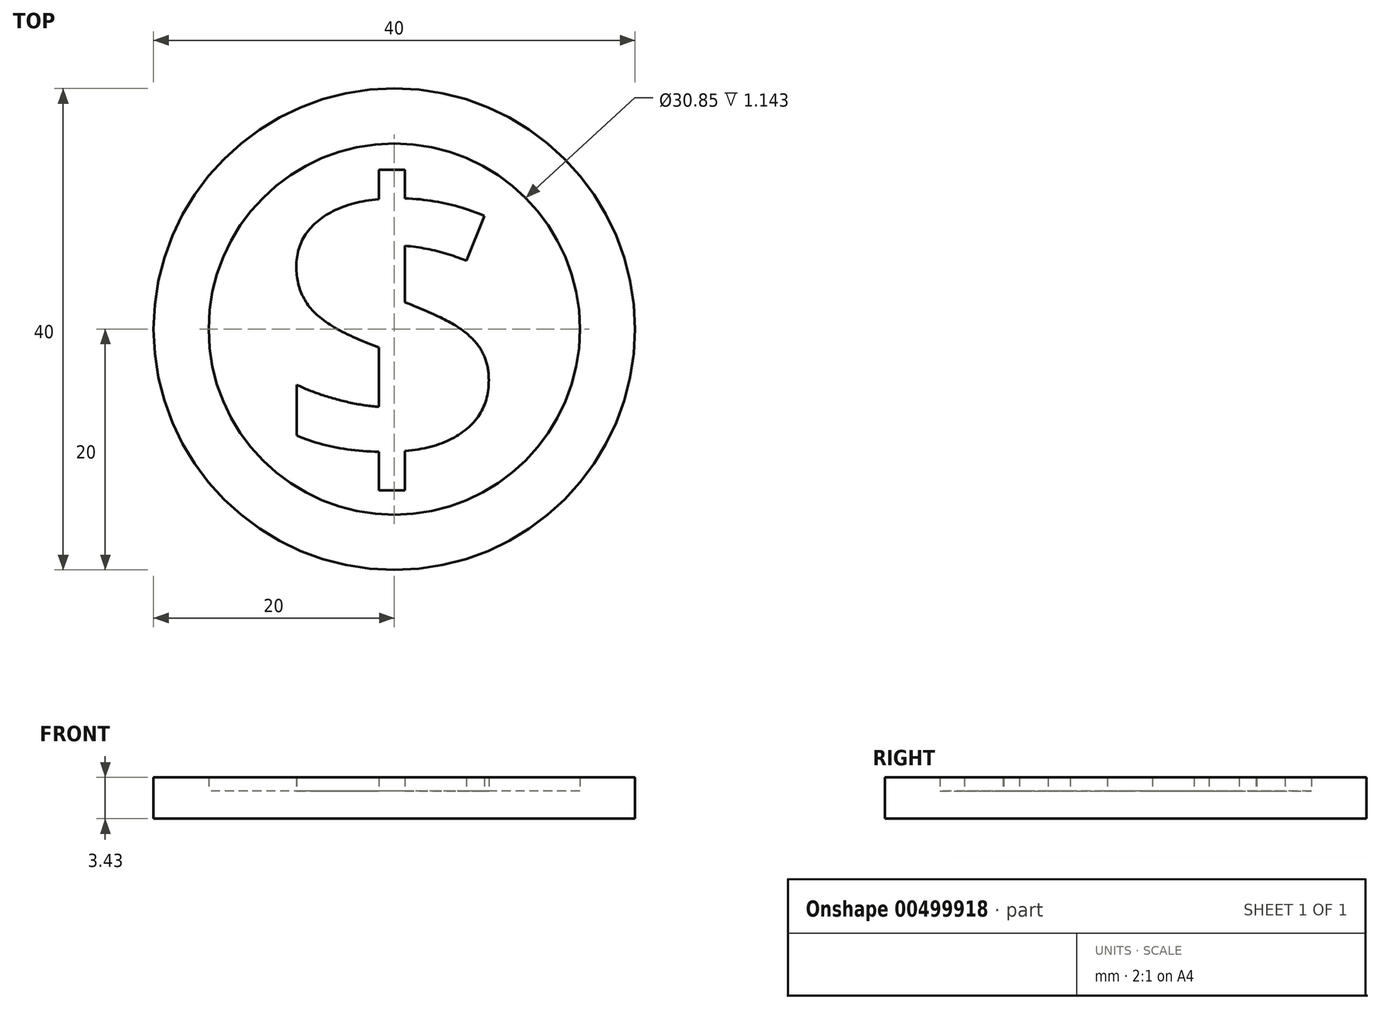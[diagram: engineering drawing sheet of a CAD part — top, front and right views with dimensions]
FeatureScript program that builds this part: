
annotation { "Feature Type Name" : "Feature", "Feature Type Description" : "" }
export const myFeature = defineFeature(function(context is Context, id is Id, definition is map)
    precondition{}
    {
        {
            var Q0;
            Q0=qCreatedBy(makeId("Top.planeOp"),FACE);
            var sketch = newSketch(context, id + "F0", { "sketchPlane" : qUnion([Q0])});
            skCircle(sketch, "E0", {"center": v(0, 0) * mm, "radius": 20 * mm});
            skSolve(sketch);
        }
        {
            var Q0;
            Q0 = qSketchRegion(id + "F0", true);
            extrude(context, id + "F1", {"entities" : qUnion([Q0]), "depth" : 2.3 * mm});
        }
        {
            var Q0;
            Q0=makeQuery(id+"F1.opExtrude","CAP_FACE",FACE,{"disambiguationData":[OSD([sQuery(id+"F0.wireOp",EDGE,"E0")])],"isStart":false});
            var sketch = newSketch(context, id + "F2", { "sketchPlane" : qUnion([Q0])});
            skText(sketch, "E1", { "text": "$", "fontName": "OpenSans-Bold.ttf"});
            const initialGuessF2  = {"E1": [-0.00954, -0.0115, 1, 0, 0.02348]};
            skSetInitialGuess(sketch, initialGuessF2);
            skSolve(sketch);
        }
        {
            var Q0;
            Q0 = qSketchRegion(id + "F2", true);
            extrude(context, id + "F3", {"entities" : qUnion([Q0]), "operationType" : NewBodyOperationType.ADD, "depth" : 1.14 * mm});
        }
        {
            var Q0;
            {var subQ0=sQuery(id+"F0.wireOp",EDGE,"E0");Q0=makeQuery(id+"F3.boolean.opBoolean","SPLIT",FACE,{"disambiguationData":[TD([makeQuery(id+"F1.opExtrude","SWEPT_FACE",FACE,{"disambiguationData":[OSD([subQ0])]})])],"derivedFrom":makeQuery(id+"F1.opExtrude","CAP_FACE",FACE,{"disambiguationData":[OSD([subQ0])],"isStart":false})});}
            var sketch = newSketch(context, id + "F4", { "sketchPlane" : qUnion([Q0])});
            skCircle(sketch, "E2.0", {"center": v(0, 0) * mm, "radius": 20 * mm});
            skCircle(sketch, "E3", {"center": v(0, 0) * mm, "radius": 15.42 * mm});
            skSolve(sketch);
        }
        {
            var Q0;
            Q0 = qSketchRegion(id + "F4", true);
            var Q1;
            Q1=makeQuery(id+"F3.opExtrude","CAP_FACE",FACE,{"disambiguationData":[OSD([sQuery(id+"F2.wireOp",EDGE,"E1.sketch_text.stroke-0"),sQuery(id+"F2.wireOp",EDGE,"E1.sketch_text.stroke-1"),sQuery(id+"F2.wireOp",EDGE,"E1.sketch_text.stroke-2"),sQuery(id+"F2.wireOp",EDGE,"E1.sketch_text.stroke-3"),sQuery(id+"F2.wireOp",EDGE,"E1.sketch_text.stroke-4"),sQuery(id+"F2.wireOp",EDGE,"E1.sketch_text.stroke-5"),sQuery(id+"F2.wireOp",EDGE,"E1.sketch_text.stroke-6"),sQuery(id+"F2.wireOp",EDGE,"E1.sketch_text.stroke-7"),sQuery(id+"F2.wireOp",EDGE,"E1.sketch_text.stroke-8"),sQuery(id+"F2.wireOp",EDGE,"E1.sketch_text.stroke-9"),sQuery(id+"F2.wireOp",EDGE,"E1.sketch_text.stroke-10"),sQuery(id+"F2.wireOp",EDGE,"E1.sketch_text.stroke-11"),sQuery(id+"F2.wireOp",EDGE,"E1.sketch_text.stroke-12"),sQuery(id+"F2.wireOp",EDGE,"E1.sketch_text.stroke-13"),sQuery(id+"F2.wireOp",EDGE,"E1.sketch_text.stroke-14"),sQuery(id+"F2.wireOp",EDGE,"E1.sketch_text.stroke-15"),sQuery(id+"F2.wireOp",EDGE,"E1.sketch_text.stroke-16"),sQuery(id+"F2.wireOp",EDGE,"E1.sketch_text.stroke-17"),sQuery(id+"F2.wireOp",EDGE,"E1.sketch_text.stroke-18"),sQuery(id+"F2.wireOp",EDGE,"E1.sketch_text.stroke-19"),sQuery(id+"F2.wireOp",EDGE,"E1.sketch_text.stroke-20"),sQuery(id+"F2.wireOp",EDGE,"E1.sketch_text.stroke-21"),sQuery(id+"F2.wireOp",EDGE,"E1.sketch_text.stroke-22"),sQuery(id+"F2.wireOp",EDGE,"E1.sketch_text.stroke-23"),sQuery(id+"F2.wireOp",EDGE,"E1.sketch_text.stroke-24"),sQuery(id+"F2.wireOp",EDGE,"E1.sketch_text.stroke-25"),sQuery(id+"F2.wireOp",EDGE,"E1.sketch_text.stroke-26"),sQuery(id+"F2.wireOp",EDGE,"E1.sketch_text.stroke-27"),sQuery(id+"F2.wireOp",EDGE,"E1.sketch_text.stroke-28"),sQuery(id+"F2.wireOp",EDGE,"E1.sketch_text.stroke-29"),sQuery(id+"F2.wireOp",EDGE,"E1.sketch_text.stroke-30"),sQuery(id+"F2.wireOp",EDGE,"E1.sketch_text.stroke-31"),sQuery(id+"F2.wireOp",EDGE,"E1.sketch_text.stroke-32")])],"isStart":false});
            extrude(context, id + "F5", {"entities" : qUnion([Q0]), "operationType" : NewBodyOperationType.ADD, "endBound" : BoundingType.UP_TO_SURFACE, "endBoundEntityFace" : qUnion([Q1]), "depth" : 3.17 * mm});
        }
        {
            var Q0;
            Q0=makeQuery(id+"F3.boolean.opBoolean","SPLIT",FACE,{"disambiguationData":[TD([makeQuery(id+"F3.opExtrude","SWEPT_FACE",FACE,{"disambiguationData":[OSD([sQuery(id+"F2.wireOp",EDGE,"E1.sketch_text.stroke-29")])]})])],"derivedFrom":makeQuery(id+"F1.opExtrude","CAP_FACE",FACE,{"disambiguationData":[OSD([sQuery(id+"F0.wireOp",EDGE,"E0")])],"isStart":false})});
            var Q1;
            Q1=makeQuery(id+"F3.boolean.opBoolean","SPLIT",FACE,{"disambiguationData":[TD([makeQuery(id+"F3.opExtrude","SWEPT_FACE",FACE,{"disambiguationData":[OSD([sQuery(id+"F2.wireOp",EDGE,"E1.sketch_text.stroke-25")])]})])],"derivedFrom":makeQuery(id+"F1.opExtrude","CAP_FACE",FACE,{"disambiguationData":[OSD([sQuery(id+"F0.wireOp",EDGE,"E0")])],"isStart":false})});
            var Q2;
            Q2=makeQuery(id+"F3.opExtrude","CAP_FACE",FACE,{"disambiguationData":[OSD([sQuery(id+"F2.wireOp",EDGE,"E1.sketch_text.stroke-0"),sQuery(id+"F2.wireOp",EDGE,"E1.sketch_text.stroke-1"),sQuery(id+"F2.wireOp",EDGE,"E1.sketch_text.stroke-2"),sQuery(id+"F2.wireOp",EDGE,"E1.sketch_text.stroke-3"),sQuery(id+"F2.wireOp",EDGE,"E1.sketch_text.stroke-4"),sQuery(id+"F2.wireOp",EDGE,"E1.sketch_text.stroke-5"),sQuery(id+"F2.wireOp",EDGE,"E1.sketch_text.stroke-6"),sQuery(id+"F2.wireOp",EDGE,"E1.sketch_text.stroke-7"),sQuery(id+"F2.wireOp",EDGE,"E1.sketch_text.stroke-8"),sQuery(id+"F2.wireOp",EDGE,"E1.sketch_text.stroke-9"),sQuery(id+"F2.wireOp",EDGE,"E1.sketch_text.stroke-10"),sQuery(id+"F2.wireOp",EDGE,"E1.sketch_text.stroke-11"),sQuery(id+"F2.wireOp",EDGE,"E1.sketch_text.stroke-12"),sQuery(id+"F2.wireOp",EDGE,"E1.sketch_text.stroke-13"),sQuery(id+"F2.wireOp",EDGE,"E1.sketch_text.stroke-14"),sQuery(id+"F2.wireOp",EDGE,"E1.sketch_text.stroke-15"),sQuery(id+"F2.wireOp",EDGE,"E1.sketch_text.stroke-16"),sQuery(id+"F2.wireOp",EDGE,"E1.sketch_text.stroke-17"),sQuery(id+"F2.wireOp",EDGE,"E1.sketch_text.stroke-18"),sQuery(id+"F2.wireOp",EDGE,"E1.sketch_text.stroke-19"),sQuery(id+"F2.wireOp",EDGE,"E1.sketch_text.stroke-20"),sQuery(id+"F2.wireOp",EDGE,"E1.sketch_text.stroke-21"),sQuery(id+"F2.wireOp",EDGE,"E1.sketch_text.stroke-22"),sQuery(id+"F2.wireOp",EDGE,"E1.sketch_text.stroke-23"),sQuery(id+"F2.wireOp",EDGE,"E1.sketch_text.stroke-24"),sQuery(id+"F2.wireOp",EDGE,"E1.sketch_text.stroke-25"),sQuery(id+"F2.wireOp",EDGE,"E1.sketch_text.stroke-26"),sQuery(id+"F2.wireOp",EDGE,"E1.sketch_text.stroke-27"),sQuery(id+"F2.wireOp",EDGE,"E1.sketch_text.stroke-28"),sQuery(id+"F2.wireOp",EDGE,"E1.sketch_text.stroke-29"),sQuery(id+"F2.wireOp",EDGE,"E1.sketch_text.stroke-30"),sQuery(id+"F2.wireOp",EDGE,"E1.sketch_text.stroke-31"),sQuery(id+"F2.wireOp",EDGE,"E1.sketch_text.stroke-32")])],"isStart":false});
            extrude(context, id + "F6", {"entities" : qUnion([Q0, Q1]), "operationType" : NewBodyOperationType.ADD, "endBound" : BoundingType.UP_TO_SURFACE, "endBoundEntityFace" : qUnion([Q2]), "depth" : 25.4 * mm});
        }
    });
